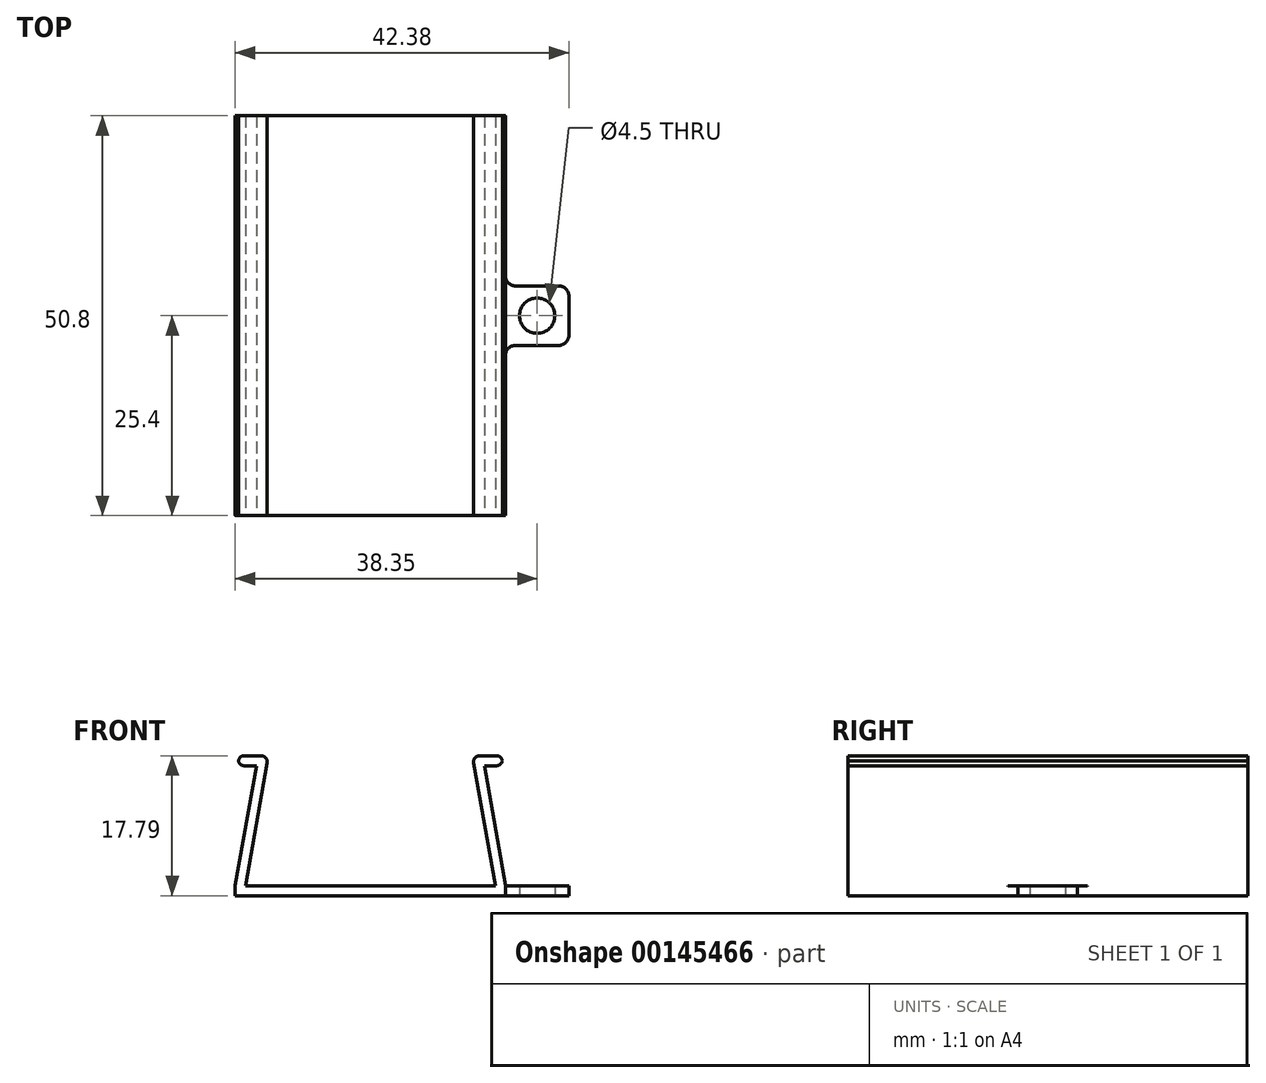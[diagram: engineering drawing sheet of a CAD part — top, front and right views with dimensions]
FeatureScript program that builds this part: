
annotation { "Feature Type Name" : "Feature", "Feature Type Description" : "" }
export const myFeature = defineFeature(function(context is Context, id is Id, definition is map)
    precondition{}
    {
        {
            var Q0;
            Q0=qCreatedBy(makeId("Front.planeOp"),FACE);
            var sketch = newSketch(context, id + "F0", { "sketchPlane" : qUnion([Q0])});
            skLineSegment(sketch, "E0.bottom", {"start": v(-17.16, 0.64) * mm, "end": v(17.16, 0.64) * mm});
            skLineSegment(sketch, "E0.top", {"start": v(-17.16, -0.64) * mm, "end": v(17.16, -0.64) * mm});
            skLineSegment(sketch, "E0.left", {"start": v(-17.16, 0.64) * mm, "end": v(-17.16, -0.64) * mm});
            skLineSegment(sketch, "E0.right", {"start": v(17.16, 0.64) * mm, "end": v(17.16, -0.64) * mm});
            skPoint(sketch, "E0.middle", {"position": v(0, 0) * mm});
            skLineSegment(sketch, "E1", {"start": v(-17.16, 0.64) * mm, "end": v(-14.48, 15.88) * mm});
            skLineSegment(sketch, "E2", {"start": v(-14.48, 15.88) * mm, "end": v(-16.77, 15.88) * mm});
            skLineSegment(sketch, "E3", {"start": v(-16.77, 15.88) * mm, "end": v(-16.77, 17.14) * mm});
            skLineSegment(sketch, "E4", {"start": v(-16.77, 17.15) * mm, "end": v(-12.96, 17.15) * mm});
            skLineSegment(sketch, "E5", {"start": v(-12.96, 17.14) * mm, "end": v(-15.88, 0.63) * mm});
            skLineSegment(sketch, "E6", {"start": v(-14.48, 15.87) * mm, "end": v(-13.23, 15.65) * mm, "construction": true});
            skLineSegment(sketch, "E7.MirrorCS", {"start": v(17.16, 0.64) * mm, "end": v(14.48, 15.88) * mm});
            skLineSegment(sketch, "E8.MirrorCS", {"start": v(14.48, 15.88) * mm, "end": v(16.77, 15.88) * mm});
            skLineSegment(sketch, "E9.MirrorCS", {"start": v(14.48, 15.87) * mm, "end": v(13.23, 15.65) * mm, "construction": true});
            skLineSegment(sketch, "E10.MirrorCS", {"start": v(12.96, 17.14) * mm, "end": v(15.88, 0.64) * mm});
            skLineSegment(sketch, "E11.MirrorCS", {"start": v(16.77, 17.15) * mm, "end": v(12.96, 17.15) * mm});
            skLineSegment(sketch, "E12.MirrorCS", {"start": v(16.77, 15.88) * mm, "end": v(16.77, 17.14) * mm});
            skSolve(sketch);
        }
        {
            var Q0;
            {var subQ0=sQuery(id+"F0.wireOp",EDGE,"E1");Q0=makeQuery(id+"F0.imprint","IMPRINT",FACE,{"disambiguationData":[TD([[makeQuery(id+"F0.imprint","IMPRINT",EDGE,{"derivedFrom":subQ0}),-1.0]])]});}
            var Q1;
            Q1=makeQuery(id+"F0.imprint","IMPRINT",FACE,{"disambiguationData":[TD([[makeQuery(id+"F0.imprint","IMPRINT",EDGE,{"derivedFrom":sQuery(id+"F0.wireOp",EDGE,"E0.top")}),1.0]])]});
            var Q2;
            {var subQ1=sQuery(id+"F0.wireOp",EDGE,"E7.MirrorCS");Q2=makeQuery(id+"F0.imprint","IMPRINT",FACE,{"disambiguationData":[TD([[makeQuery(id+"F0.imprint","IMPRINT",EDGE,{"derivedFrom":subQ1}),1.0]])]});}
            extrude(context, id + "F1", {"entities" : qUnion([Q0, Q1, Q2]), "endBound" : BoundingType.SYMMETRIC, "oppositeDirection" : true, "depth" : 50.8 * mm});
        }
        {
            var Q0;
            Q0=makeQuery(id+"F1.opExtrude","SWEPT_EDGE",EDGE,{"disambiguationData":[OSD([sQuery(id+"F0.wireOp",EDGE,"E4"),sQuery(id+"F0.wireOp",EDGE,"E5")])]});
            var Q1;
            Q1=makeQuery(id+"F1.opExtrude","SWEPT_EDGE",EDGE,{"disambiguationData":[OSD([sQuery(id+"F0.wireOp",EDGE,"E3"),sQuery(id+"F0.wireOp",EDGE,"E4")])]});
            var Q2;
            Q2=makeQuery(id+"F1.opExtrude","SWEPT_EDGE",EDGE,{"disambiguationData":[OSD([sQuery(id+"F0.wireOp",EDGE,"E11.MirrorCS"),sQuery(id+"F0.wireOp",EDGE,"E12.MirrorCS")])]});
            var Q3;
            Q3=makeQuery(id+"F1.opExtrude","SWEPT_EDGE",EDGE,{"disambiguationData":[OSD([sQuery(id+"F0.wireOp",EDGE,"E10.MirrorCS"),sQuery(id+"F0.wireOp",EDGE,"E11.MirrorCS")])]});
            var Q4;
            Q4=makeQuery(id+"F1.opExtrude","SWEPT_EDGE",EDGE,{"disambiguationData":[OSD([sQuery(id+"F0.wireOp",EDGE,"E2"),sQuery(id+"F0.wireOp",EDGE,"E3")])]});
            var Q5;
            Q5=makeQuery(id+"F1.opExtrude","SWEPT_EDGE",EDGE,{"disambiguationData":[OSD([sQuery(id+"F0.wireOp",EDGE,"E8.MirrorCS"),sQuery(id+"F0.wireOp",EDGE,"E12.MirrorCS")])]});
            var Q6;
            Q6=makeQuery(id+"F1.opExtrude","SWEPT_EDGE",EDGE,{"disambiguationData":[OSD([sQuery(id+"F0.wireOp",EDGE,"E0.bottom"),sQuery(id+"F0.wireOp",EDGE,"E0.left"),sQuery(id+"F0.wireOp",EDGE,"E1")])]});
            var Q7;
            Q7=makeQuery(id+"F1.opExtrude","SWEPT_EDGE",EDGE,{"disambiguationData":[OSD([sQuery(id+"F0.wireOp",EDGE,"E0.bottom"),sQuery(id+"F0.wireOp",EDGE,"E0.right"),sQuery(id+"F0.wireOp",EDGE,"E7.MirrorCS")])]});
            fillet(context, id + "F2", {"entities" : qUnion([Q0, Q1, Q2, Q3, Q4, Q5, Q6, Q7]), "radius" : 0.76 * mm, "tangentPropagation" : true, "allowEdgeOverflow" : false});
        }
        {
            var Q0;
            Q0=makeQuery(id+"F1.opExtrude","SWEPT_FACE",FACE,{"disambiguationData":[OSD([sQuery(id+"F0.wireOp",EDGE,"E0.top")])]});
            var sketch = newSketch(context, id + "F3", { "sketchPlane" : qUnion([Q0])});
            skLineSegment(sketch, "E13.bottom", {"start": v(18.43, 3.77) * mm, "end": v(23.95, 3.77) * mm});
            skLineSegment(sketch, "E13.top", {"start": v(18.43, -3.77) * mm, "end": v(23.95, -3.77) * mm});
            skLineSegment(sketch, "E13.left", {"start": v(17.16, 3.77) * mm, "end": v(17.16, -3.77) * mm});
            skLineSegment(sketch, "E13.right", {"start": v(25.22, 2.5) * mm, "end": v(25.22, -2.5) * mm});
            skPoint(sketch, "E13.middle", {"position": v(21.2, 0) * mm});
            skPoint(sketch, "E13.middle.positionSnap0", {"position": v(17.16, 0) * mm});
            skPoint(sketch, "E13.centerSnap0", {"position": v(17.16, 0) * mm});
            skCircle(sketch, "E14", {"center": v(21.2, 0) * mm, "radius": 2.25 * mm});
            skPoint(sketch, "E15.visualSharp", {"position": v(25.22, 3.77) * mm});
            skArc(sketch, "E15.filletArc", {"start": v(25.22, 2.5) * mm, "mid": v(24.84, 3.4) * mm, "end": v(23.95, 3.77) * mm});
            skPoint(sketch, "E16.visualSharp", {"position": v(25.22, -3.77) * mm});
            skArc(sketch, "E16.filletArc", {"start": v(23.95, -3.77) * mm, "mid": v(24.84, -3.4) * mm, "end": v(25.22, -2.5) * mm});
            skLineSegment(sketch, "E17", {"start": v(17.16, 5.04) * mm, "end": v(17.16, 25.4) * mm});
            skLineSegment(sketch, "E18", {"start": v(17.16, -5.04) * mm, "end": v(17.16, -25.4) * mm});
            skPoint(sketch, "E19.visualSharp", {"position": v(17.16, -3.77) * mm});
            skArc(sketch, "E19.filletArc", {"start": v(18.43, -3.77) * mm, "mid": v(17.54, -4.14) * mm, "end": v(17.16, -5.04) * mm});
            skPoint(sketch, "E20.visualSharp", {"position": v(17.16, 3.77) * mm});
            skArc(sketch, "E20.filletArc", {"start": v(17.16, 5.04) * mm, "mid": v(17.54, 4.14) * mm, "end": v(18.43, 3.77) * mm});
            skArc(sketch, "E21.MirrorCS", {"start": v(-17.16, 5.04) * mm, "mid": v(-17.54, 4.14) * mm, "end": v(-18.43, 3.77) * mm});
            skArc(sketch, "E22.MirrorCS", {"start": v(-18.43, -3.77) * mm, "mid": v(-17.54, -4.14) * mm, "end": v(-17.16, -5.04) * mm});
            skArc(sketch, "E23.MirrorCS", {"start": v(-25.22, 2.5) * mm, "mid": v(-24.84, 3.4) * mm, "end": v(-23.95, 3.77) * mm});
            skPoint(sketch, "E24.MirrorP", {"position": v(-17.16, 0) * mm});
            skArc(sketch, "E25.MirrorCS", {"start": v(-23.95, -3.77) * mm, "mid": v(-24.84, -3.4) * mm, "end": v(-25.22, -2.5) * mm});
            skLineSegment(sketch, "E26.MirrorCS", {"start": v(-18.43, 3.77) * mm, "end": v(-23.95, 3.77) * mm});
            skCircle(sketch, "E27.MirrorC", {"center": v(-21.2, 0) * mm, "radius": 2.25 * mm});
            skLineSegment(sketch, "E28.MirrorCS", {"start": v(-18.43, -3.77) * mm, "end": v(-23.95, -3.77) * mm});
            skPoint(sketch, "E29.MirrorP", {"position": v(-17.16, 3.77) * mm});
            skLineSegment(sketch, "E30.MirrorCS", {"start": v(-17.16, 3.77) * mm, "end": v(-17.16, -3.77) * mm});
            skLineSegment(sketch, "E31.MirrorCS", {"start": v(-25.22, 2.5) * mm, "end": v(-25.22, -2.5) * mm});
            skPoint(sketch, "E32.MirrorP", {"position": v(-17.16, -3.77) * mm});
            skPoint(sketch, "E33.MirrorP", {"position": v(-25.22, -3.77) * mm});
            skPoint(sketch, "E34.MirrorP", {"position": v(-25.22, 3.77) * mm});
            skSolve(sketch);
        }
        {
            var Q0;
            {var subQ0=sQuery(id+"F3.wireOp",EDGE,"E21.MirrorCS");Q0=makeQuery(id+"F3.imprint","IMPRINT",FACE,{"disambiguationData":[TD([[makeQuery(id+"F3.imprint","IMPRINT",EDGE,{"derivedFrom":subQ0}),1.0]])]});}
            var Q1;
            Q1=makeQuery(id+"F3.imprint","IMPRINT",FACE,{"disambiguationData":[TD([[makeQuery(id+"F3.imprint","IMPRINT",EDGE,{"derivedFrom":sQuery(id+"F3.wireOp",EDGE,"E13.bottom")}),-1.0]])]});
            extrude(context, id + "F4", {"entities" : qUnion([Q0, Q1]), "operationType" : NewBodyOperationType.ADD, "oppositeDirection" : true, "depth" : 1.27 * mm});
        }
    });
